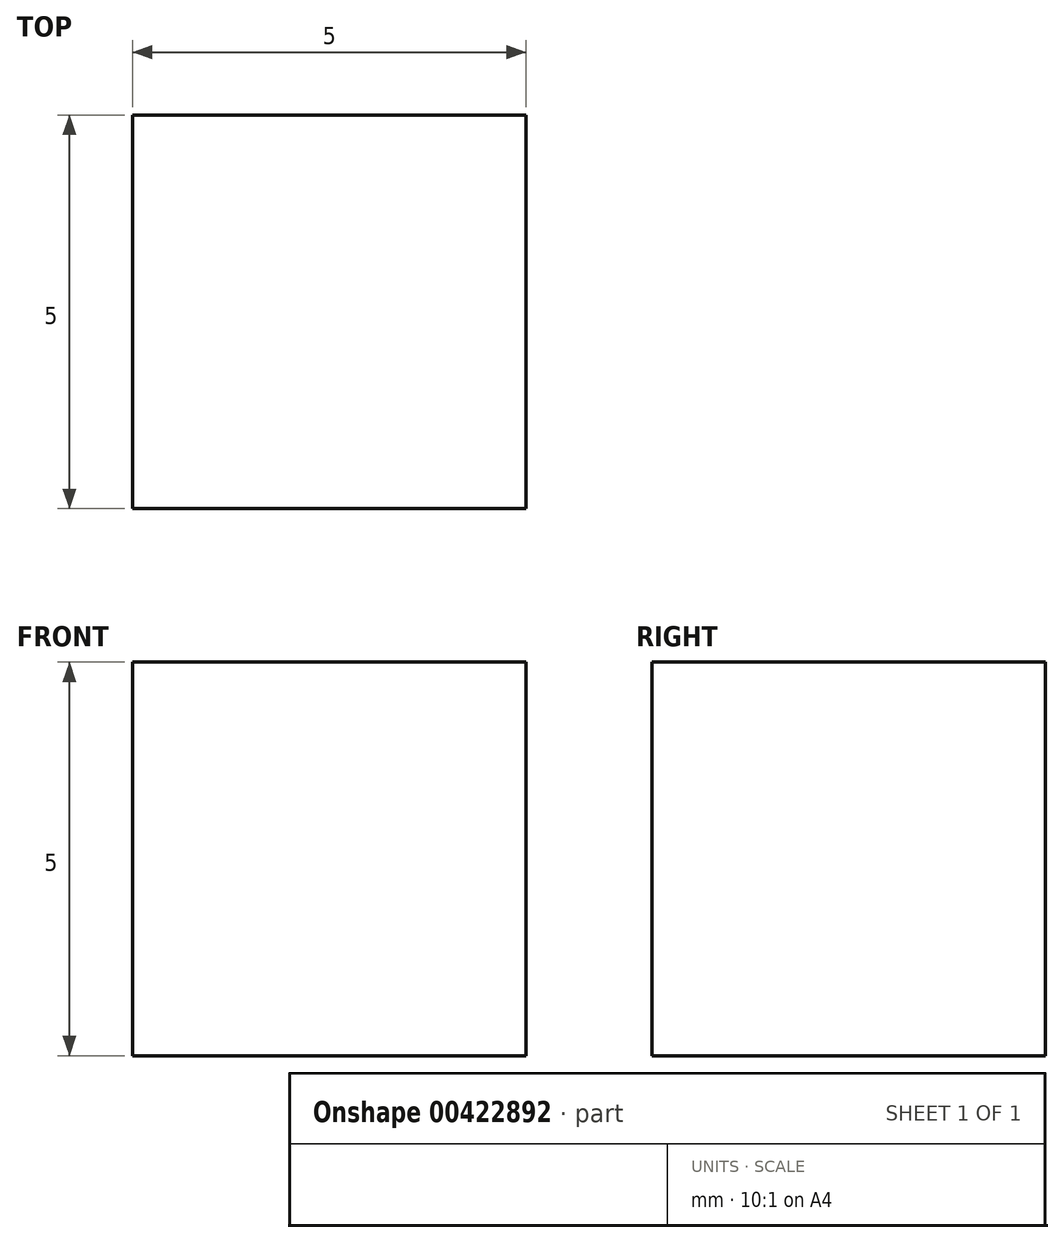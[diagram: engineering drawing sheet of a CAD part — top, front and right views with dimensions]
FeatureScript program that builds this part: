
annotation { "Feature Type Name" : "Feature", "Feature Type Description" : "" }
export const myFeature = defineFeature(function(context is Context, id is Id, definition is map)
    precondition{}
    {
        {
            var Q0;
            Q0=qCreatedBy(makeId("Top.planeOp"),FACE);
            var sketch = newSketch(context, id + "F0", { "sketchPlane" : qUnion([Q0])});
            skLineSegment(sketch, "E0.bottom", {"start": v(2.5, -2.5) * mm, "end": v(-2.5, -2.5) * mm});
            skLineSegment(sketch, "E0.top", {"start": v(2.5, 2.5) * mm, "end": v(-2.5, 2.5) * mm});
            skLineSegment(sketch, "E0.left", {"start": v(2.5, -2.5) * mm, "end": v(2.5, 2.5) * mm});
            skLineSegment(sketch, "E0.right", {"start": v(-2.5, -2.5) * mm, "end": v(-2.5, 2.5) * mm});
            skPoint(sketch, "E0.middle", {"position": v(0, 0) * mm});
            skSolve(sketch);
        }
        {
            var Q0;
            Q0 = qSketchRegion(id + "F0", true);
            extrude(context, id + "F1", {"entities" : qUnion([Q0]), "endBound" : BoundingType.SYMMETRIC, "depth" : 5 * mm});
        }
    });
